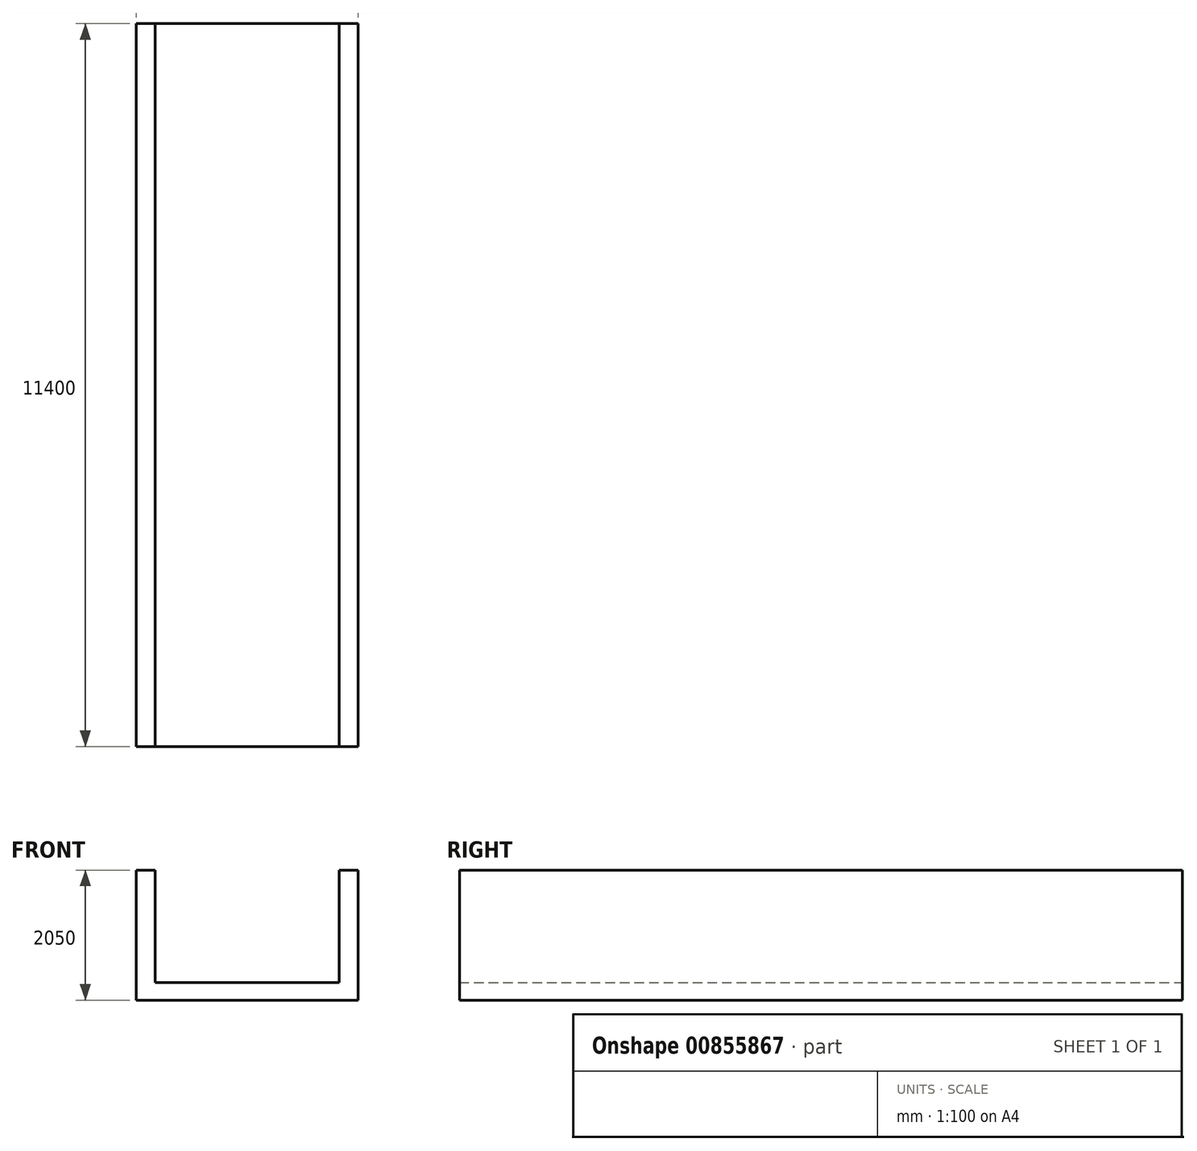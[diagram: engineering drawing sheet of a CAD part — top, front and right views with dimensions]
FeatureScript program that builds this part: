
annotation { "Feature Type Name" : "Feature", "Feature Type Description" : "" }
export const myFeature = defineFeature(function(context is Context, id is Id, definition is map)
    precondition{}
    {
        {
            var Q0;
            Q0=qCreatedBy(makeId("Front.planeOp"),FACE);
            var sketch = newSketch(context, id + "F0", { "sketchPlane" : qUnion([Q0])});
            skLineSegment(sketch, "E0", {"start": v(-502.56, 1596.88) * mm, "end": v(-502.56, -453.12) * mm});
            skLineSegment(sketch, "E1", {"start": v(-502.56, -453.12) * mm, "end": v(1247.44, -453.12) * mm});
            skLineSegment(sketch, "E2", {"start": v(1247.44, -453.12) * mm, "end": v(1247.44, -174.55) * mm, "construction": true});
            skLineSegment(sketch, "E3", {"start": v(1247.44, -174.55) * mm, "end": v(-202.56, -174.55) * mm});
            skLineSegment(sketch, "E4", {"start": v(-202.56, -174.55) * mm, "end": v(-202.56, 1596.88) * mm});
            skLineSegment(sketch, "E5", {"start": v(-202.56, 1596.88) * mm, "end": v(-502.56, 1596.88) * mm});
            skLineSegment(sketch, "E6.MirrorCS", {"start": v(1247.44, -174.55) * mm, "end": v(2697.44, -174.55) * mm});
            skLineSegment(sketch, "E7.MirrorCS", {"start": v(2697.44, -174.55) * mm, "end": v(2697.44, 1596.88) * mm});
            skLineSegment(sketch, "E8.MirrorCS", {"start": v(2697.44, 1596.88) * mm, "end": v(2997.44, 1596.88) * mm});
            skLineSegment(sketch, "E9.MirrorCS", {"start": v(2997.44, 1596.88) * mm, "end": v(2997.44, -453.12) * mm});
            skLineSegment(sketch, "E10.MirrorCS", {"start": v(2997.44, -453.12) * mm, "end": v(1247.44, -453.12) * mm});
            skSolve(sketch);
        }
        {
            var Q0;
            Q0=makeQuery(id+"F0.imprint","IMPRINT",FACE,{"disambiguationData":[TD([[makeQuery(id+"F0.imprint","IMPRINT",EDGE,{"derivedFrom":sQuery(id+"F0.wireOp",EDGE,"E0")}),1.0]])]});
            extrude(context, id + "F1", {"entities" : qUnion([Q0]), "endBound" : BoundingType.SYMMETRIC, "depth" : 11400 * mm, "offsetDistance" : 25 * mm});
        }
    });
